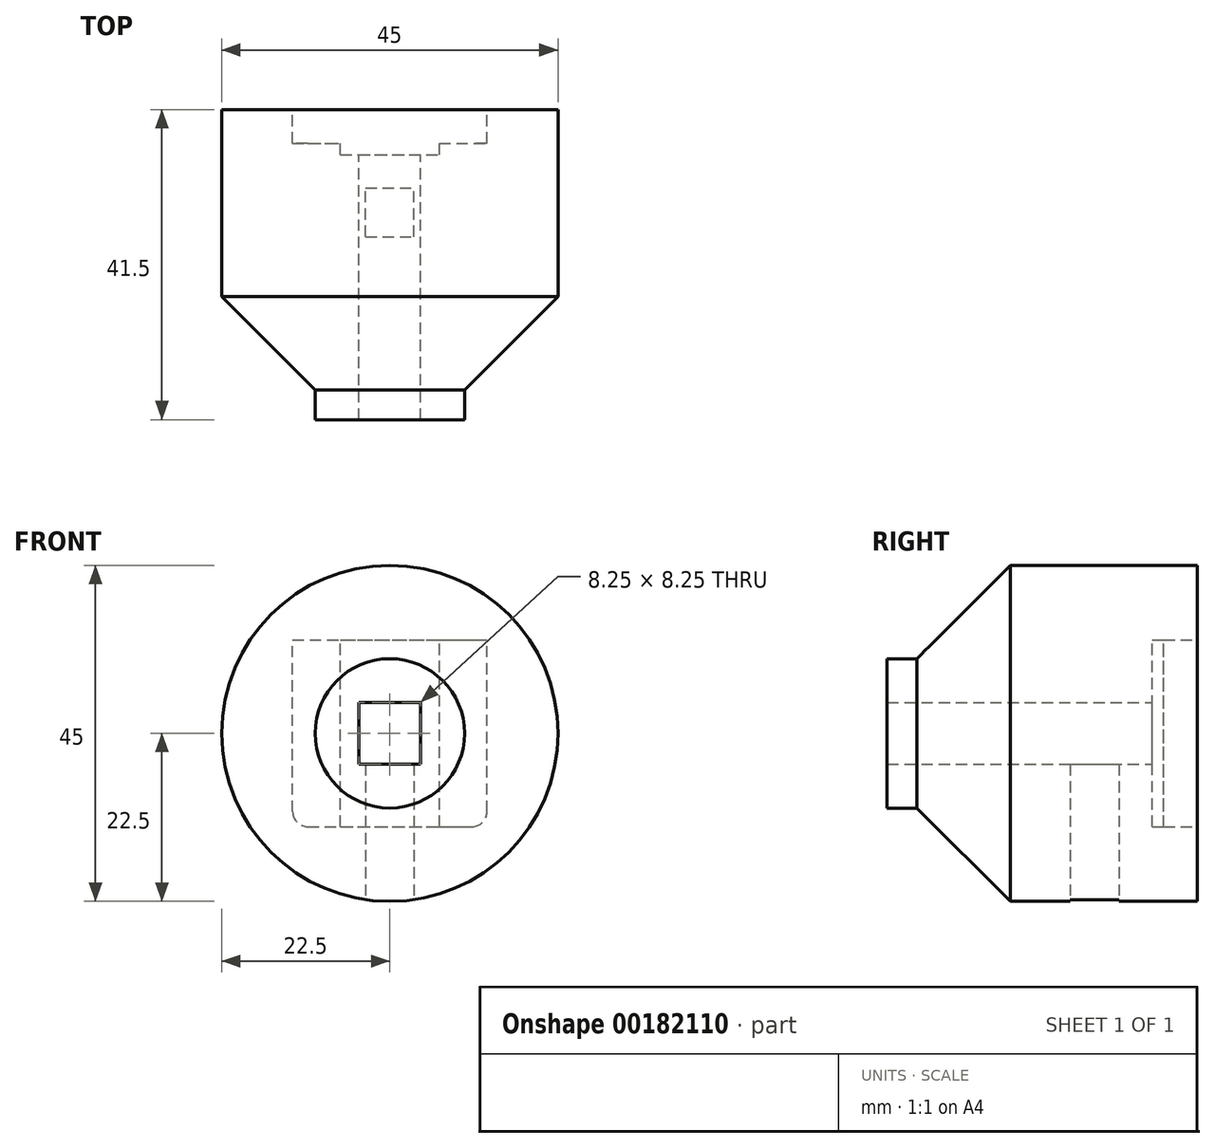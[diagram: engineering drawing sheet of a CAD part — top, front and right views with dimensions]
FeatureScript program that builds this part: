
annotation { "Feature Type Name" : "Feature", "Feature Type Description" : "" }
export const myFeature = defineFeature(function(context is Context, id is Id, definition is map)
    precondition{}
    {
        {
            var Q0;
            Q0=qCreatedBy(makeId("Top.planeOp"),FACE);
            var sketch = newSketch(context, id + "F0", { "sketchPlane" : qUnion([Q0])});
            skLineSegment(sketch, "E0.bottom", {"start": v(22.5, -12.5) * mm, "end": v(-22.5, -12.5) * mm});
            skLineSegment(sketch, "E0.top", {"start": v(22.5, 12.5) * mm, "end": v(-22.5, 12.5) * mm});
            skLineSegment(sketch, "E0.left", {"start": v(22.5, -12.5) * mm, "end": v(22.5, 12.5) * mm});
            skLineSegment(sketch, "E0.right", {"start": v(-22.5, -12.5) * mm, "end": v(-22.5, 12.5) * mm});
            skPoint(sketch, "E0.middle", {"position": v(0, 0) * mm});
            skLineSegment(sketch, "E1.bottom", {"start": v(10, -29) * mm, "end": v(-10, -29) * mm});
            skLineSegment(sketch, "E1.top", {"start": v(10, -25) * mm, "end": v(-10, -25) * mm});
            skLineSegment(sketch, "E1.left", {"start": v(10, -29) * mm, "end": v(10, -25) * mm});
            skLineSegment(sketch, "E1.right", {"start": v(-10, -29) * mm, "end": v(-10, -25) * mm});
            skPoint(sketch, "E1.middle", {"position": v(0, -27) * mm});
            skLineSegment(sketch, "E2", {"start": v(-22.5, -12.5) * mm, "end": v(-10, -25) * mm});
            skLineSegment(sketch, "E3", {"start": v(22.5, -12.5) * mm, "end": v(10, -25) * mm});
            skLineSegment(sketch, "E4", {"start": v(0, 12.5) * mm, "end": v(0, -29) * mm});
            skSolve(sketch);
        }
        {
            var Q0;
            {var subQ0=sQuery(id+"F0.wireOp",EDGE,"E1.right");Q0=makeQuery(id+"F0.imprint","IMPRINT",FACE,{"disambiguationData":[TD([[makeQuery(id+"F0.imprint","IMPRINT",EDGE,{"derivedFrom":subQ0}),-1.0]])]});}
            var Q1;
            {var subQ0=sQuery(id+"F0.wireOp",EDGE,"E2");Q1=makeQuery(id+"F0.imprint","IMPRINT",FACE,{"disambiguationData":[TD([[makeQuery(id+"F0.imprint","IMPRINT",EDGE,{"derivedFrom":subQ0}),1.0]])]});}
            var Q2;
            {var subQ0=sQuery(id+"F0.wireOp",EDGE,"E0.right");Q2=makeQuery(id+"F0.imprint","IMPRINT",FACE,{"disambiguationData":[TD([[makeQuery(id+"F0.imprint","IMPRINT",EDGE,{"derivedFrom":subQ0}),-1.0]])]});}
            var Q3;
            Q3=sQuery(id+"F0.wireOp",EDGE,"E4");
            revolve(context, id + "F1", {"entities" : qUnion([Q0, Q1, Q2]), "axis" : qUnion([Q3]), "revolveType" : RevolveType.FULL});
        }
        {
            var Q0;
            Q0=makeQuery(id+"F1.opRevolve","SWEPT_FACE",FACE,{"disambiguationData":[OSD([sQuery(id+"F0.wireOp",EDGE,"E0.top")])]});
            var sketch = newSketch(context, id + "F2", { "sketchPlane" : qUnion([Q0])});
            skLineSegment(sketch, "E5.bottom", {"start": v(4.12, -4.12) * mm, "end": v(-4.12, -4.13) * mm});
            skLineSegment(sketch, "E5.top", {"start": v(4.12, 4.13) * mm, "end": v(-4.12, 4.12) * mm});
            skLineSegment(sketch, "E5.left", {"start": v(4.12, -4.12) * mm, "end": v(4.12, 4.13) * mm});
            skLineSegment(sketch, "E5.right", {"start": v(-4.12, -4.13) * mm, "end": v(-4.12, 4.12) * mm});
            skPoint(sketch, "E5.middle", {"position": v(0, 0) * mm});
            skLineSegment(sketch, "E6.bottom", {"start": v(13, -12.5) * mm, "end": v(-13, -12.5) * mm});
            skLineSegment(sketch, "E6.top", {"start": v(13, 12.5) * mm, "end": v(-13, 12.5) * mm});
            skLineSegment(sketch, "E6.left", {"start": v(13, -12.5) * mm, "end": v(13, 12.5) * mm});
            skLineSegment(sketch, "E6.right", {"start": v(-13, -12.5) * mm, "end": v(-13, 12.5) * mm});
            skLineSegment(sketch, "E7.bottom", {"start": v(6.62, -12.5) * mm, "end": v(-6.63, -12.5) * mm});
            skLineSegment(sketch, "E7.top", {"start": v(6.62, 12.5) * mm, "end": v(-6.63, 12.5) * mm});
            skLineSegment(sketch, "E7.left", {"start": v(6.62, -12.5) * mm, "end": v(6.62, 12.5) * mm});
            skLineSegment(sketch, "E7.right", {"start": v(-6.62, -12.5) * mm, "end": v(-6.62, 12.5) * mm});
            skLineSegment(sketch, "E8.bottom", {"start": v(-13, -12.5) * mm, "end": v(13, -12.5) * mm});
            skLineSegment(sketch, "E8.top", {"start": v(-13, -22.5) * mm, "end": v(13, -22.5) * mm});
            skLineSegment(sketch, "E8.left", {"start": v(-13, -12.5) * mm, "end": v(-13, -22.5) * mm});
            skLineSegment(sketch, "E8.right", {"start": v(13, -12.5) * mm, "end": v(13, -22.5) * mm});
            skLineSegment(sketch, "E9", {"start": v(0, 0) * mm, "end": v(16.22, -15.6) * mm, "construction": true});
            skLineSegment(sketch, "E10", {"start": v(0, 0) * mm, "end": v(0, 22.5) * mm, "construction": true});
            skLineSegment(sketch, "E11", {"start": v(0, 0) * mm, "end": v(-16.22, -15.6) * mm, "construction": true});
            skSolve(sketch);
        }
        {
            var Q0;
            Q0=makeQuery(id+"F2.imprint","IMPRINT",FACE,{"disambiguationData":[TD([[makeQuery(id+"F2.imprint","IMPRINT",EDGE,{"derivedFrom":sQuery(id+"F2.wireOp",EDGE,"E5.bottom")}),-1.0]])]});
            extrude(context, id + "F3", {"entities" : qUnion([Q0]), "operationType" : NewBodyOperationType.REMOVE, "endBound" : BoundingType.THROUGH_ALL, "oppositeDirection" : true, "depth" : 25 * mm});
        }
        {
            var Q0;
            Q0=makeQuery(id+"F2.imprint","IMPRINT",FACE,{"disambiguationData":[TD([[makeQuery(id+"F2.imprint","IMPRINT",EDGE,{"derivedFrom":sQuery(id+"F2.wireOp",EDGE,"E5.bottom")}),1.0]])]});
            extrude(context, id + "F4", {"entities" : qUnion([Q0]), "operationType" : NewBodyOperationType.REMOVE, "oppositeDirection" : true, "depth" : 6 * mm});
        }
        {
            var Q0;
            {var subQ0=sQuery(id+"F2.wireOp",EDGE,"E6.right");Q0=makeQuery(id+"F2.imprint","IMPRINT",FACE,{"disambiguationData":[TD([[makeQuery(id+"F2.imprint","IMPRINT",EDGE,{"derivedFrom":subQ0}),-1.0]])]});}
            var Q1;
            {var subQ0=sQuery(id+"F2.wireOp",EDGE,"E6.left");Q1=makeQuery(id+"F2.imprint","IMPRINT",FACE,{"disambiguationData":[TD([[makeQuery(id+"F2.imprint","IMPRINT",EDGE,{"derivedFrom":subQ0}),1.0]])]});}
            var Q2;
            {var subQ1=sQuery(id+"F2.wireOp",EDGE,"E8.bottom");var subQ3=makeQuery(id+"F2.imprint","INTERSECT",VERTEX,{"derivedFrom":[sQuery(id+"F2.wireOp",EDGE,"E7.left"),subQ1]});Q2=makeQuery(id+"F2.imprint","IMPRINT",FACE,{"disambiguationData":[TD([[makeQuery(id+"F2.imprint","IMPRINT",EDGE,{"disambiguationData":[TD([[subQ3,1.0]])],"derivedFrom":subQ1}),-1.0]])]});}
            extrude(context, id + "F5", {"entities" : qUnion([Q0, Q1, Q2]), "operationType" : NewBodyOperationType.REMOVE, "oppositeDirection" : true, "depth" : 4.5 * mm});
        }
        {
            var Q0;
            Q0=makeQuery(id+"F5.boolean.opBoolean","COPY",EDGE,{"derivedFrom":makeQuery(id+"F5.opExtrude","SWEPT_EDGE",EDGE,{"disambiguationData":[OSD([sQuery(id+"F0.wireOp",EDGE,"E0.top"),sQuery(id+"F0.wireOp",EDGE,"E0.right"),sQuery(id+"F2.wireOp",EDGE,"E8.left")])]})});
            var Q1;
            Q1=makeQuery(id+"F5.boolean.opBoolean","COPY",EDGE,{"derivedFrom":makeQuery(id+"F5.opExtrude","SWEPT_EDGE",EDGE,{"disambiguationData":[OSD([sQuery(id+"F0.wireOp",EDGE,"E0.top"),sQuery(id+"F0.wireOp",EDGE,"E0.right"),sQuery(id+"F2.wireOp",EDGE,"E8.right")])]})});
            fillet(context, id + "F6", {"entities" : qUnion([Q0, Q1]), "radius" : 2 * mm, "tangentPropagation" : true, "allowEdgeOverflow" : false});
        }
        {
            var Q0;
            Q0=qCreatedBy(makeId("Top.planeOp"),FACE);
            cPlane(context, id + "F7", {"entities" : qUnion([Q0]), "cplaneType" : CPlaneType.OFFSET, "offset" : 25 * mm, "oppositeDirection" : true, "width" : 150 * mm, "height" : 150 * mm});
        }
        {
            var Q0;
            Q0=qCreatedBy(id+"F7.planeOp",FACE);
            var sketch = newSketch(context, id + "F8", { "sketchPlane" : qUnion([Q0])});
            skLineSegment(sketch, "E12.bottom", {"start": v(3.25, 2) * mm, "end": v(-3.25, 2) * mm});
            skLineSegment(sketch, "E12.top", {"start": v(3.25, -4.5) * mm, "end": v(-3.25, -4.5) * mm});
            skLineSegment(sketch, "E12.left", {"start": v(3.25, 2) * mm, "end": v(3.25, -4.5) * mm});
            skLineSegment(sketch, "E12.right", {"start": v(-3.25, 2) * mm, "end": v(-3.25, -4.5) * mm});
            skPoint(sketch, "E12.middle", {"position": v(0, -1.25) * mm});
            skSolve(sketch);
        }
        {
            var Q0;
            Q0 = qSketchRegion(id + "F8", true);
            extrude(context, id + "F9", {"entities" : qUnion([Q0]), "operationType" : NewBodyOperationType.REMOVE, "depth" : 25 * mm});
        }
    });
